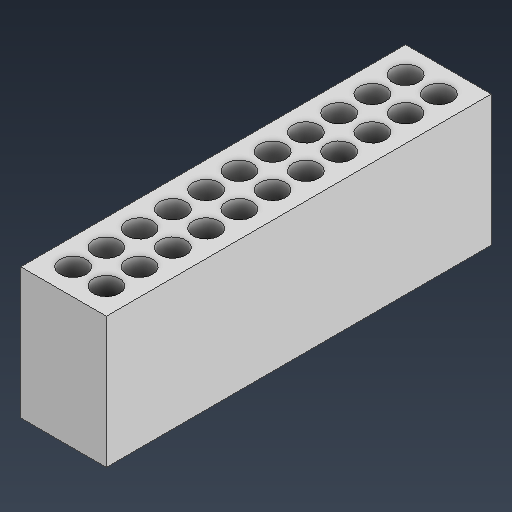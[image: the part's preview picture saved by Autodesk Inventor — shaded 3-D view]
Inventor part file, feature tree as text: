
AUTODESK INVENTOR PART (.ipt)
format: ipt  version: 2025.3 (Build 293356000, 356)  size: 165,376 bytes
history: native  units: mm
features: sketch x2, extrude x1
ambient origin geometry x8: Origin, YZ Plane, XZ Plane, XY Plane, X Axis, Y Axis, Z Axis, Center Point
bodies: Solid1 (feature_tree)
feature tree (3):
  extrude  "Extrusion1"  Depth=2.54mm
  sketch  "Sketch1"  dims[d0=2.0mm d1=20.0mm d3=2.54mm d4=110.0mm d6=2.54mm]
  sketch  "Sketch Rectangular Pattern1"  dims[d9=1.0mm d10=1.0mm d11=1.0mm d12=1.0mm d13=10.0mm d14=0.0mm]
